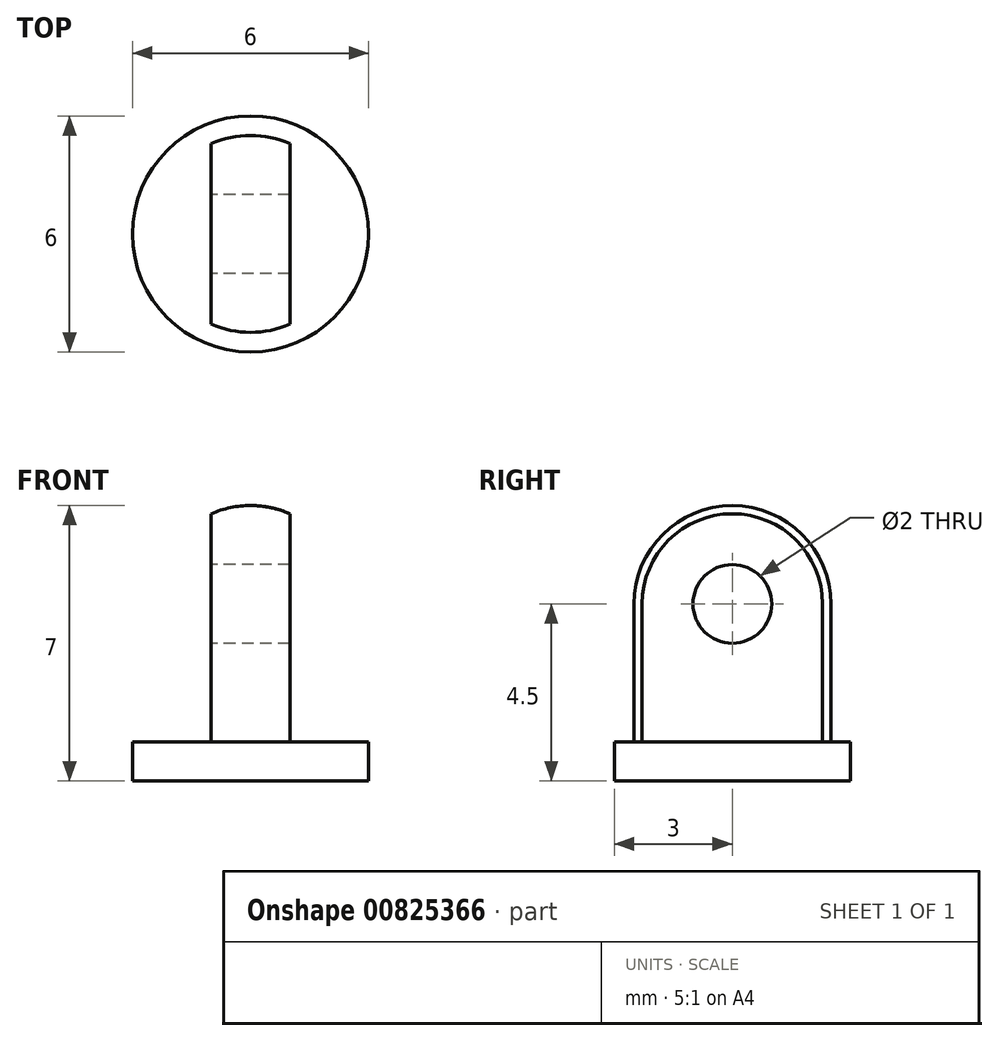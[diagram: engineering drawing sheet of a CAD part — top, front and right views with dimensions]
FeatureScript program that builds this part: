
annotation { "Feature Type Name" : "Feature", "Feature Type Description" : "" }
export const myFeature = defineFeature(function(context is Context, id is Id, definition is map)
    precondition{}
    {
        {
            var Q0;
            Q0=qCreatedBy(makeId("Top.planeOp"),FACE);
            var sketch = newSketch(context, id + "F0", { "sketchPlane" : qUnion([Q0])});
            skCircle(sketch, "E0", {"center": v(0, 0) * mm, "radius": 3 * mm});
            skSolve(sketch);
        }
        {
            var Q0;
            Q0 = qSketchRegion(id + "F0", true);
            extrude(context, id + "F1", {"entities" : qUnion([Q0]), "depth" : 1 * mm, "offsetDistance" : 25 * mm});
        }
        {
            var Q0;
            Q0=makeQuery(id+"F1.opExtrude","CAP_FACE",FACE,{"disambiguationData":[OSD([sQuery(id+"F0.wireOp",EDGE,"E0")])],"isStart":false});
            var sketch = newSketch(context, id + "F2", { "sketchPlane" : qUnion([Q0])});
            skCircle(sketch, "E1", {"center": v(0, 0) * mm, "radius": 2.5 * mm});
            skSolve(sketch);
        }
        {
            var Q0;
            Q0 = qSketchRegion(id + "F2", true);
            extrude(context, id + "F3", {"entities" : qUnion([Q0]), "operationType" : NewBodyOperationType.ADD, "depth" : 6 * mm, "offsetDistance" : 25 * mm});
        }
        {
            var Q0;
            Q0=makeQuery(id+"F3.opExtrude","CAP_EDGE",EDGE,{"disambiguationData":[OSD([sQuery(id+"F2.wireOp",EDGE,"E1")])],"isStart":false});
            fillet(context, id + "F4", {"entities" : qUnion([Q0]), "radius" : 2.5 * mm, "tangentPropagation" : true, "allowEdgeOverflow" : false});
        }
        {
            var Q0;
            Q0=qCreatedBy(makeId("Front.planeOp"),FACE);
            var sketch = newSketch(context, id + "F5", { "sketchPlane" : qUnion([Q0])});
            skLineSegment(sketch, "E2", {"start": v(0, 0) * mm, "end": v(0, 1) * mm, "construction": true});
            skLineSegment(sketch, "E3", {"start": v(0, 1) * mm, "end": v(1, 1) * mm, "construction": true});
            skLineSegment(sketch, "E4", {"start": v(0, 1) * mm, "end": v(-1, 1) * mm, "construction": true});
            skLineSegment(sketch, "E5.bottom", {"start": v(1, 1) * mm, "end": v(3.04, 1) * mm});
            skLineSegment(sketch, "E5.top", {"start": v(1, 7.26) * mm, "end": v(3.04, 7.26) * mm});
            skLineSegment(sketch, "E5.left", {"start": v(1, 1) * mm, "end": v(1, 7.26) * mm});
            skLineSegment(sketch, "E5.right", {"start": v(3.04, 1) * mm, "end": v(3.04, 7.26) * mm});
            skLineSegment(sketch, "E6.bottom", {"start": v(-1, 1) * mm, "end": v(-3.07, 1) * mm});
            skLineSegment(sketch, "E6.top", {"start": v(-1, 7.25) * mm, "end": v(-3.07, 7.25) * mm});
            skLineSegment(sketch, "E6.left", {"start": v(-1, 1) * mm, "end": v(-1, 7.25) * mm});
            skLineSegment(sketch, "E6.right", {"start": v(-3.07, 1) * mm, "end": v(-3.07, 7.25) * mm});
            skSolve(sketch);
        }
        {
            var Q0;
            Q0 = qSketchRegion(id + "F5", true);
            extrude(context, id + "F6", {"entities" : qUnion([Q0]), "operationType" : NewBodyOperationType.REMOVE, "endBound" : BoundingType.SYMMETRIC, "oppositeDirection" : true, "depth" : 25 * mm, "offsetDistance" : 25 * mm});
        }
        {
            var Q0;
            Q0=makeQuery(id+"F6.boolean.opBoolean","COPY",FACE,{"derivedFrom":makeQuery(id+"F6.opExtrude","SWEPT_FACE",FACE,{"disambiguationData":[OSD([sQuery(id+"F5.wireOp",EDGE,"E6.left")])]})});
            var sketch = newSketch(context, id + "F7", { "sketchPlane" : qUnion([Q0])});
            skCircle(sketch, "E7", {"center": v(0, 4.5) * mm, "radius": 1 * mm});
            skSolve(sketch);
        }
        {
            var Q0;
            Q0 = qSketchRegion(id + "F7", true);
            extrude(context, id + "F8", {"entities" : qUnion([Q0]), "operationType" : NewBodyOperationType.REMOVE, "oppositeDirection" : true, "depth" : 25 * mm, "offsetDistance" : 25 * mm});
        }
    });
